# Revit family: E5IX_15_1122_11
name_source: partatom
category: Structural Connections
revit_build: Autodesk Revit 2016 (Build: 20150220_1215(x64)
units: mm (PartAtom-declared; Revit-internal decimal feet)

## family parameters
Always vertical = No
Cut with Voids When Loaded = No
Enable cutting in views = No
Material for Model Behavior = Steel
OmniClass Number = 23.20.40.11.24.14
OmniClass Title = Wood Connectors
Shared = No
Work Plane-Based = Yes

## types (1)
- E5IX_15_1122_11
    Default Elevation = 0 mm  [stored 0 ft]
    Density = 0.09 kg
    Description = Angle brackets
    EPD = https://www.strongtie.eu
    ETA / DoP = https://www.strongtie.eu
    Manufacturer = Simpson Strong-Tie
    Model = E5IX/1.5/1122/11
    Model Disclaimer = Contact Simpson Strong-Tie Company  for more information
    Model ID = 0295243156341001886441836208709376660248
    Name = E5IX/1.5/1122/11
    ObjectType = E5IX/1.5/1122/11
    Product Material = Stainless steel A4
    Product Type = Angle brackets
    Reference = E5IX/1.5/1122/11
    Technical datasheet = https://www.strongtie.eu
    URL = www.strongtie.eu
    UniClass Number = Pr_20_85_09_09
    UniClass Title = Bracketed angle supports

note: [stored X ft] marks values corroborated as IEEE doubles in the binary element streams (Revit-internal decimal feet)

## geometry (parser evidence)
native form markers: Blend x25, Sweep x3
no freeform markers — native parametric forms only
